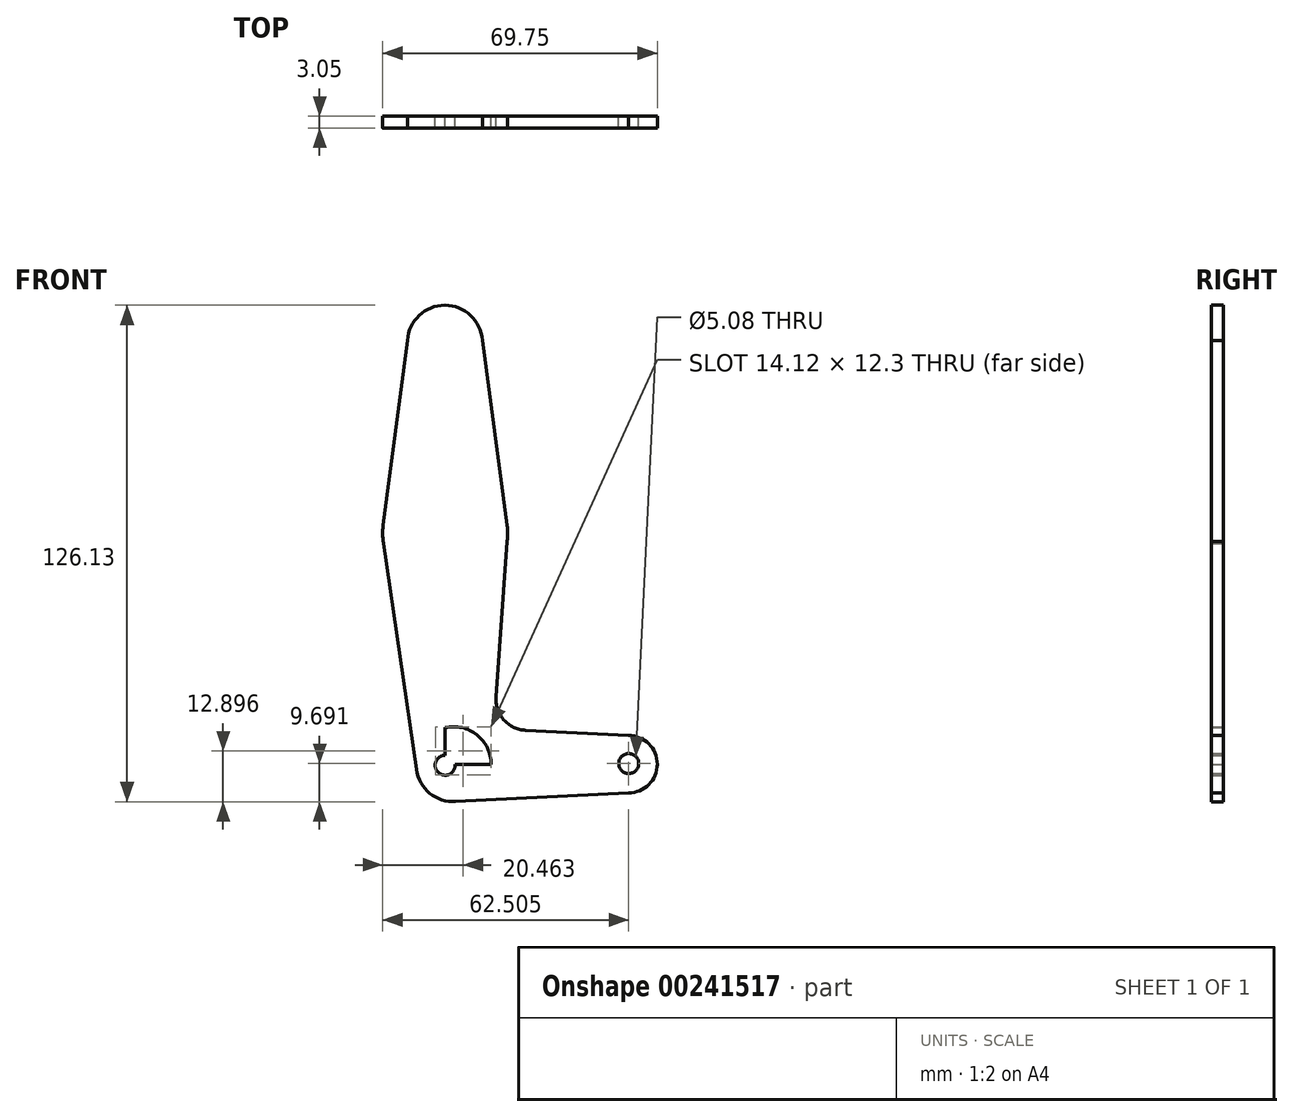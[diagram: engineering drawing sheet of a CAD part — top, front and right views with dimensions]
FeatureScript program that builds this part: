
annotation { "Feature Type Name" : "Feature", "Feature Type Description" : "" }
export const myFeature = defineFeature(function(context is Context, id is Id, definition is map)
    precondition{}
    {
        {
            var Q0;
            Q0=qCreatedBy(makeId("Front.planeOp"),FACE);
            var sketch = newSketch(context, id + "F0", { "sketchPlane" : qUnion([Q0])});
            skLineSegment(sketch, "E0", {"start": v(-46.58, 64.35) * mm, "end": v(-46.58, -43.6) * mm});
            skCircle(sketch, "E1", {"center": v(-44.45, -43.34) * mm, "radius": 9.52 * mm});
            skCircle(sketch, "E2", {"center": v(-46.64, 63.75) * mm, "radius": 9.53 * mm});
            skCircle(sketch, "E3", {"center": v(-46.58, 15.36) * mm, "radius": 15.88 * mm});
            skLineSegment(sketch, "E4", {"start": v(-44.45, -43.34) * mm, "end": v(0, -43.34) * mm});
            skCircle(sketch, "E5", {"center": v(0, -43.34) * mm, "radius": 7.3 * mm});
            skLineSegment(sketch, "E6", {"start": v(-56.14, 64.35) * mm, "end": v(-62.32, 17.43) * mm});
            skLineSegment(sketch, "E7", {"start": v(-37.13, 64.35) * mm, "end": v(-30.84, 17.47) * mm});
            skLineSegment(sketch, "E8", {"start": v(-62.34, 13.43) * mm, "end": v(-53.88, -44.71) * mm});
            skLineSegment(sketch, "E9", {"start": v(-30.84, 13.25) * mm, "end": v(-33.67, -26.21) * mm});
            skLineSegment(sketch, "E10", {"start": v(0, -50.64) * mm, "end": v(-46.58, -52.98) * mm});
            skLineSegment(sketch, "E11", {"start": v(0, -36.04) * mm, "end": v(-26.14, -34.72) * mm});
            skCircle(sketch, "E12", {"center": v(-46.58, -43.6) * mm, "radius": 2.54 * mm});
            skCircle(sketch, "E13", {"center": v(0.06, -43.17) * mm, "radius": 2.54 * mm});
            skPoint(sketch, "E14.newPointA", {"position": v(-46.58, -33.7) * mm});
            skArc(sketch, "E14.filletArc", {"start": v(-33.67, -26.21) * mm, "mid": v(-31.7, -32.05) * mm, "end": v(-26.14, -34.72) * mm});
            skLineSegment(sketch, "E15", {"start": v(-46.58, -43.6) * mm, "end": v(-44.45, -43.34) * mm});
            skSolve(sketch);
        }
        {
            var Q0;
            Q0 = qSketchRegion(id + "F0", true);
            extrude(context, id + "F1", {"entities" : qUnion([Q0]), "depth" : 3.05 * mm});
        }
    });
